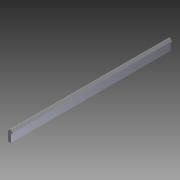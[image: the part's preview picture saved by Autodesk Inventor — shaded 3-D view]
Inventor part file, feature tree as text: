
AUTODESK INVENTOR PART (.ipt)
format: ipt  version: 2014 (Build 180170000, 170)  size: 94,720 bytes
history: native  units: in
note: dims shown in document units (in); Inventor stores cm internally (conversion verified against a paired STEP export)
features: fillet x1, other x1, imported_body x1
ambient origin geometry x8: Origin, YZ Plane, XZ Plane, XY Plane, X Axis, Y Axis, Z Axis, Center Point
bodies: Body1 (feature_tree)
feature tree (3):
  fillet  "Fillet1"  [1 undecoded]
  other  "BWC-T3-11"
  imported_body  "Base1"
note: 1 required parameter value undecoded (feature->parameter linkage not recoverable at this tier; creation-order binding heuristic only, values carry confidence <= 0.55)
